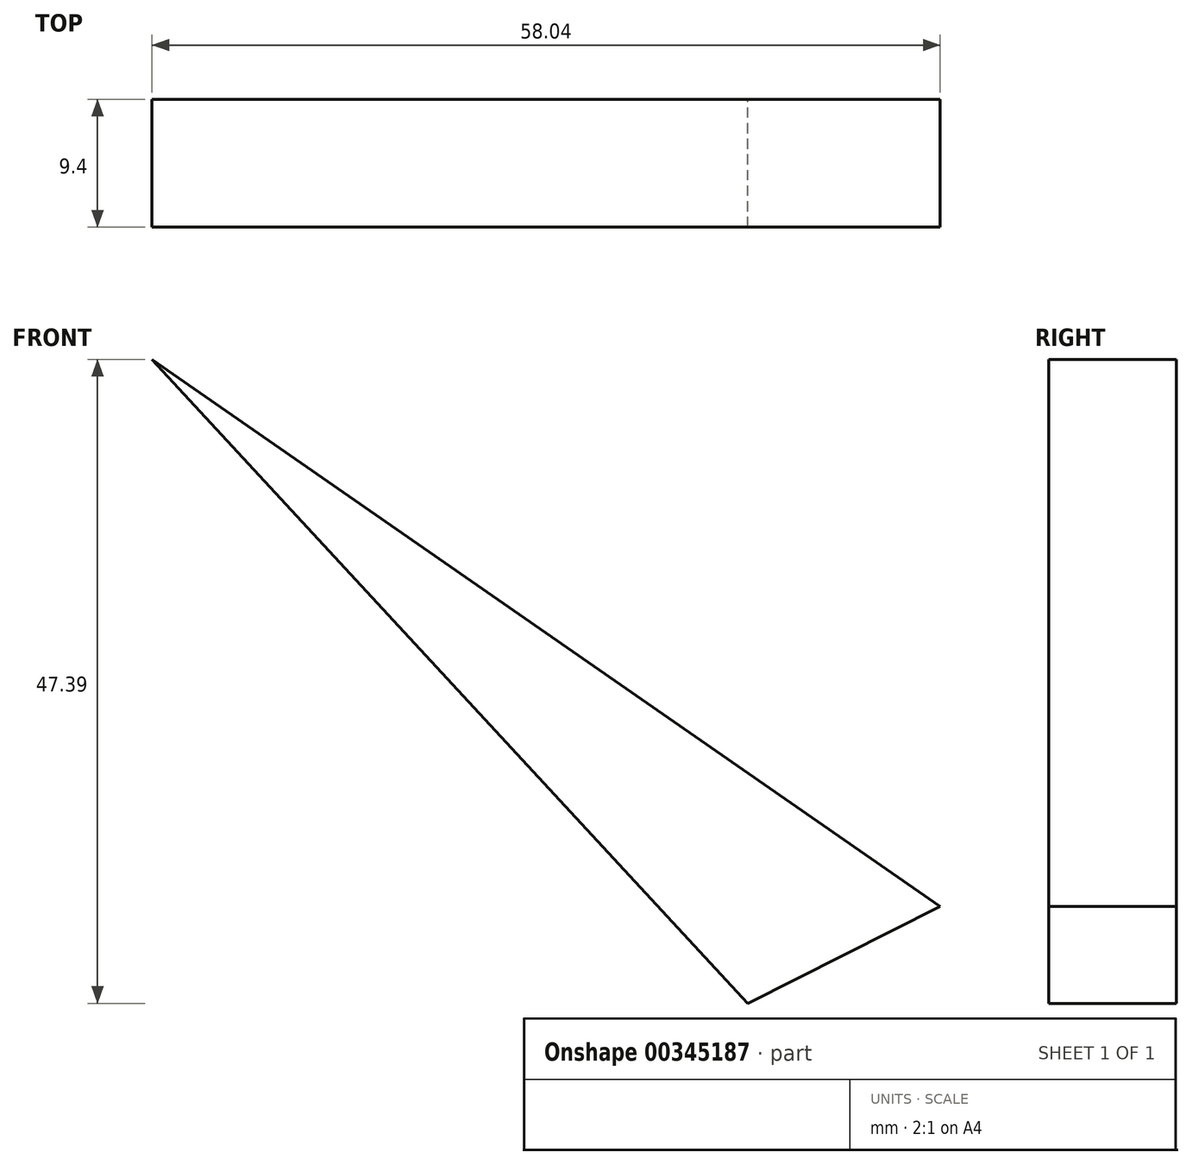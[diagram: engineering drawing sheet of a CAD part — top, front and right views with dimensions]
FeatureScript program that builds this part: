
annotation { "Feature Type Name" : "Feature", "Feature Type Description" : "" }
export const myFeature = defineFeature(function(context is Context, id is Id, definition is map)
    precondition{}
    {
        {
            var Q0;
            Q0=qCreatedBy(makeId("Front.planeOp"),FACE);
            var sketch = newSketch(context, id + "F0", { "sketchPlane" : qUnion([Q0])});
            skLineSegment(sketch, "E0", {"start": v(58.04, 0) * mm, "end": v(0, 40.27) * mm});
            skLineSegment(sketch, "E1", {"start": v(0, 40.27) * mm, "end": v(43.86, -7.12) * mm});
            skLineSegment(sketch, "E2", {"start": v(43.86, -7.12) * mm, "end": v(58.04, 0) * mm});
            skSolve(sketch);
        }
        {
            var Q0;
            Q0 = qSketchRegion(id + "F0", true);
            extrude(context, id + "F1", {"entities" : qUnion([Q0]), "depth" : 9.4 * mm});
        }
    });
